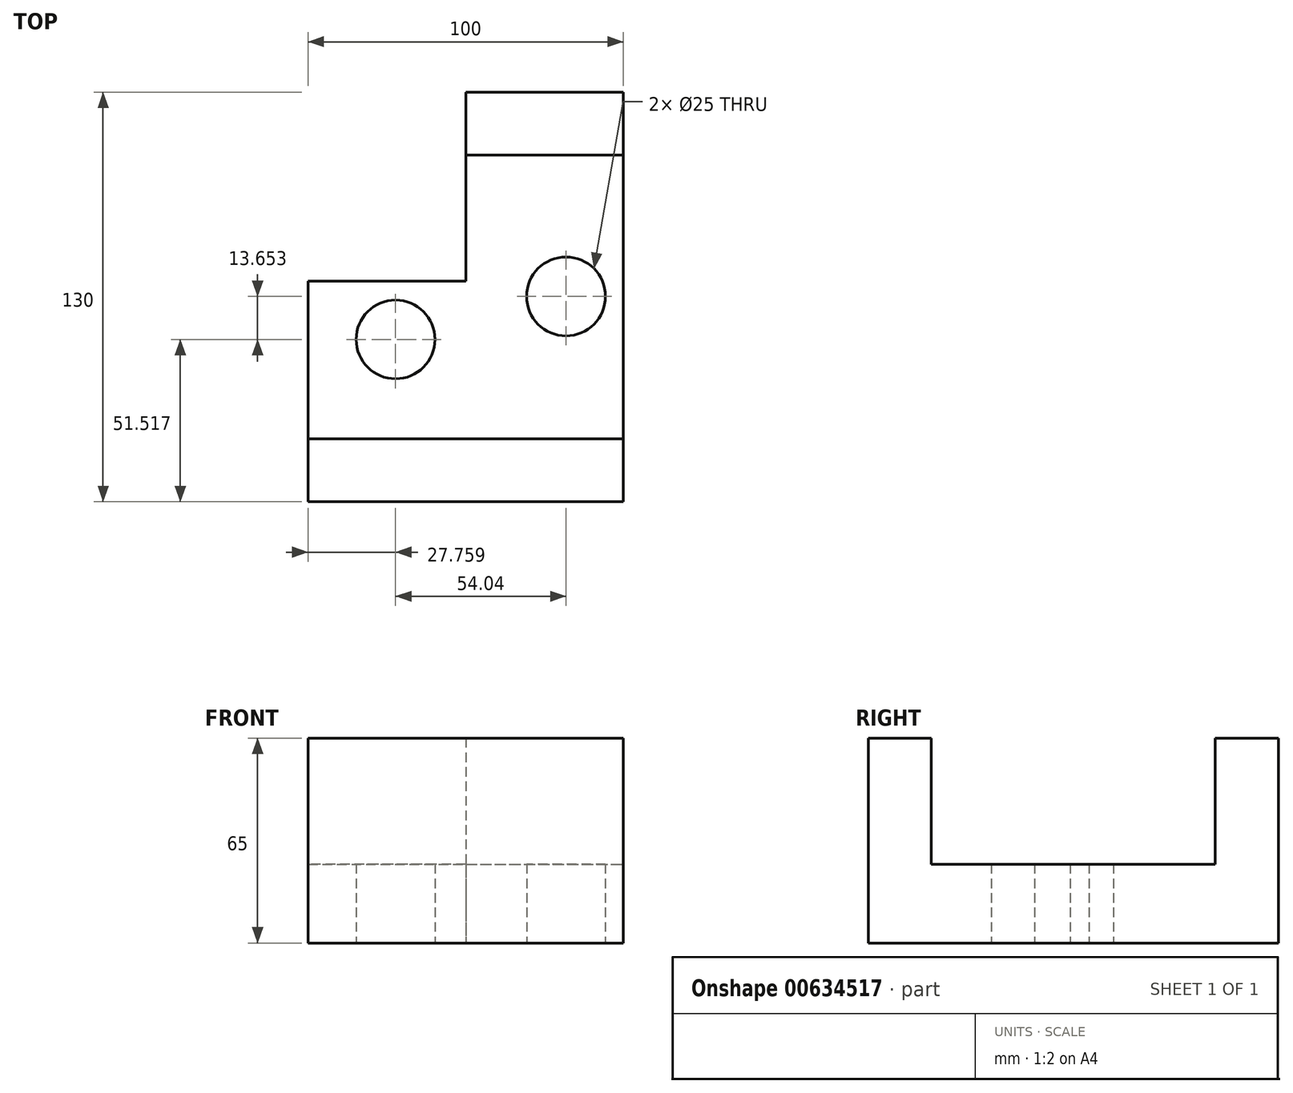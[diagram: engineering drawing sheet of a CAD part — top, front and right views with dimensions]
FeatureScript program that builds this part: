
annotation { "Feature Type Name" : "Feature", "Feature Type Description" : "" }
export const myFeature = defineFeature(function(context is Context, id is Id, definition is map)
    precondition{}
    {
        {
            var Q0;
            Q0=qCreatedBy(makeId("Top.planeOp"),FACE);
            var sketch = newSketch(context, id + "F0", { "sketchPlane" : qUnion([Q0])});
            skLineSegment(sketch, "E0.bottom", {"start": v(53.05, -65.17) * mm, "end": v(-46.95, -65.17) * mm});
            skLineSegment(sketch, "E0.top", {"start": v(3.05, 4.83) * mm, "end": v(-46.95, 4.83) * mm});
            skLineSegment(sketch, "E0.left", {"start": v(53.05, -65.17) * mm, "end": v(53.05, 4.83) * mm});
            skLineSegment(sketch, "E0.right", {"start": v(-46.95, -65.17) * mm, "end": v(-46.95, 4.83) * mm});
            skLineSegment(sketch, "E1.top", {"start": v(53.05, 64.83) * mm, "end": v(3.05, 64.83) * mm});
            skLineSegment(sketch, "E1.left", {"start": v(53.05, 4.83) * mm, "end": v(53.05, 64.83) * mm});
            skLineSegment(sketch, "E1.right", {"start": v(3.05, 4.83) * mm, "end": v(3.05, 64.83) * mm});
            skCircle(sketch, "E2", {"center": v(34.85, 0) * mm, "radius": 12.5 * mm});
            skCircle(sketch, "E3", {"center": v(-19.2, -13.65) * mm, "radius": 12.5 * mm});
            skSolve(sketch);
        }
        {
            var Q0;
            Q0 = qSketchRegion(id + "F0", true);
            extrude(context, id + "F1", {"entities" : qUnion([Q0]), "depth" : 25 * mm, "offsetDistance" : 25 * mm});
        }
        {
            var Q0;
            Q0=makeQuery(id+"F1.opExtrude","CAP_FACE",FACE,{"disambiguationData":[OSD([sQuery(id+"F0.wireOp",EDGE,"E0.bottom"),sQuery(id+"F0.wireOp",EDGE,"E0.top"),sQuery(id+"F0.wireOp",EDGE,"E0.left"),sQuery(id+"F0.wireOp",EDGE,"E0.right"),sQuery(id+"F0.wireOp",EDGE,"E1.top"),sQuery(id+"F0.wireOp",EDGE,"E1.left"),sQuery(id+"F0.wireOp",EDGE,"E1.right"),sQuery(id+"F0.wireOp",EDGE,"E2"),sQuery(id+"F0.wireOp",EDGE,"E3")])],"isStart":false});
            var sketch = newSketch(context, id + "F2", { "sketchPlane" : qUnion([Q0])});
            skLineSegment(sketch, "E4", {"start": v(3.05, 44.83) * mm, "end": v(53.05, 44.83) * mm});
            skLineSegment(sketch, "E5", {"start": v(53.05, 44.83) * mm, "end": v(53.05, 64.83) * mm});
            skLineSegment(sketch, "E6", {"start": v(53.05, 64.83) * mm, "end": v(3.05, 64.83) * mm});
            skLineSegment(sketch, "E7", {"start": v(3.05, 64.83) * mm, "end": v(3.05, 44.83) * mm});
            skLineSegment(sketch, "E8", {"start": v(-46.95, -45.17) * mm, "end": v(53.05, -45.17) * mm});
            skLineSegment(sketch, "E9", {"start": v(53.05, -45.17) * mm, "end": v(53.05, -65.17) * mm});
            skLineSegment(sketch, "E10", {"start": v(53.05, -65.17) * mm, "end": v(-46.95, -65.17) * mm});
            skLineSegment(sketch, "E11", {"start": v(-46.95, -65.17) * mm, "end": v(-46.95, -45.17) * mm});
            skSolve(sketch);
        }
        {
            var Q0;
            Q0=makeQuery(id+"F2.imprint","IMPRINT",FACE,{"disambiguationData":[TD([[makeQuery(id+"F2.imprint","IMPRINT",EDGE,{"derivedFrom":sQuery(id+"F2.wireOp",EDGE,"E8")}),-1.0]])]});
            var Q1;
            Q1=makeQuery(id+"F2.imprint","IMPRINT",FACE,{"disambiguationData":[TD([[makeQuery(id+"F2.imprint","IMPRINT",EDGE,{"derivedFrom":sQuery(id+"F2.wireOp",EDGE,"E4")}),1.0]])]});
            extrude(context, id + "F3", {"entities" : qUnion([Q0, Q1]), "operationType" : NewBodyOperationType.ADD, "depth" : 40 * mm, "offsetDistance" : 25 * mm});
        }
    });
